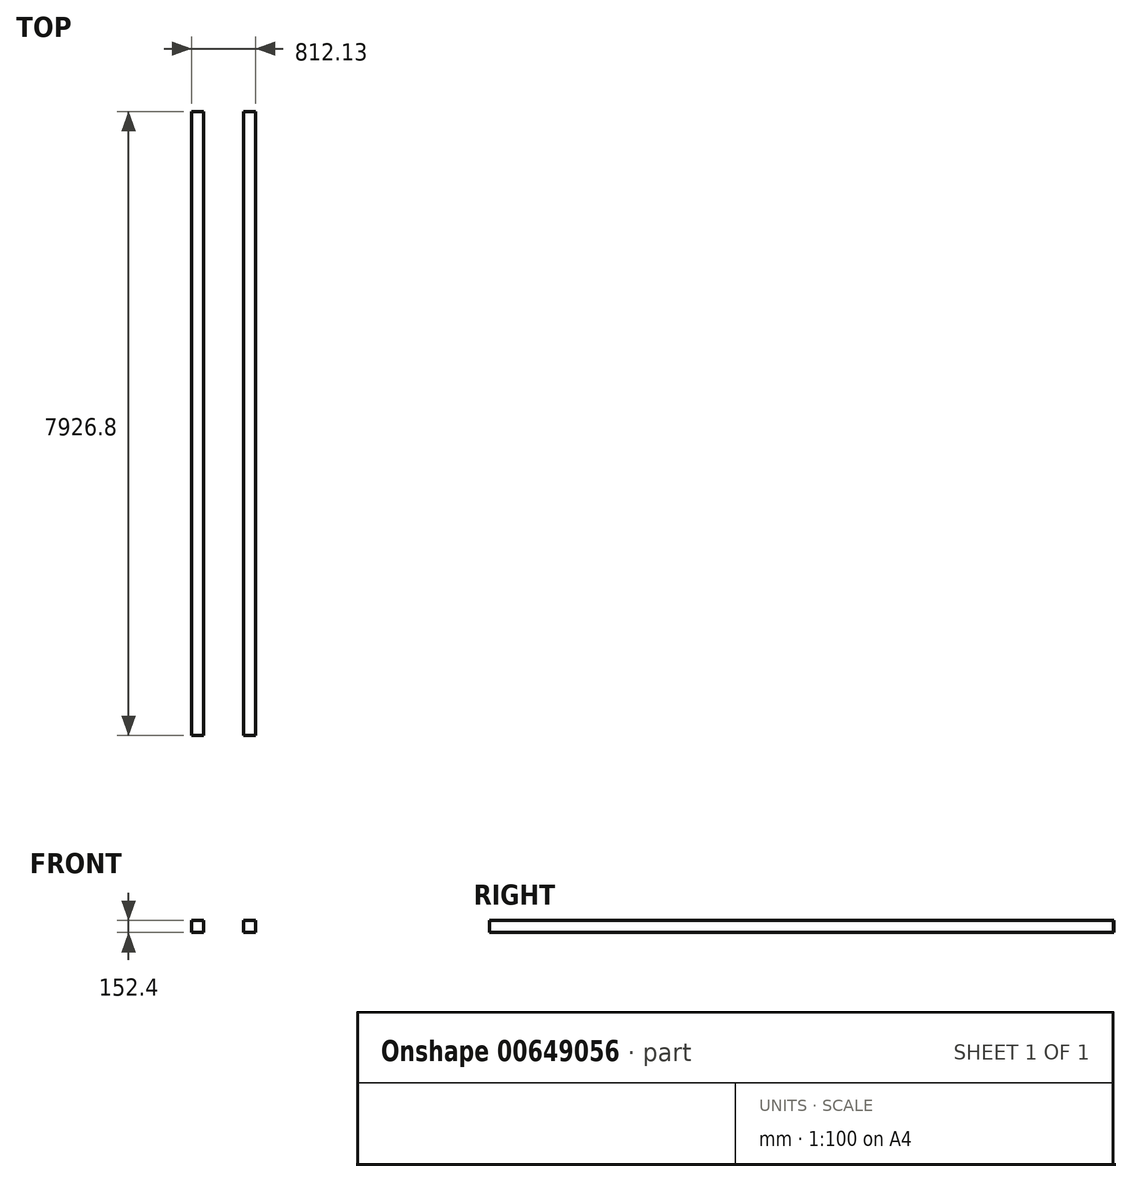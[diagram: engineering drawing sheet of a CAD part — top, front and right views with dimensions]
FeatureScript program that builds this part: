
annotation { "Feature Type Name" : "Feature", "Feature Type Description" : "" }
export const myFeature = defineFeature(function(context is Context, id is Id, definition is map)
    precondition{}
    {
        {
            var Q0;
            Q0=qCreatedBy(makeId("Top.planeOp"),FACE);
            var sketch = newSketch(context, id + "F0", { "sketchPlane" : qUnion([Q0])});
            skLineSegment(sketch, "E0.bottom", {"start": v(-434.17, 7458.07) * mm, "end": v(-281.77, 7458.07) * mm});
            skLineSegment(sketch, "E0.top", {"start": v(-434.17, -466.73) * mm, "end": v(-281.77, -466.73) * mm});
            skLineSegment(sketch, "E0.left", {"start": v(-434.17, 7458.07) * mm, "end": v(-434.17, -466.73) * mm});
            skLineSegment(sketch, "E0.right", {"start": v(-281.77, 7458.07) * mm, "end": v(-281.77, -466.73) * mm});
            skLineSegment(sketch, "E1.bottom", {"start": v(225.56, 7456.07) * mm, "end": v(377.96, 7456.07) * mm});
            skLineSegment(sketch, "E1.top", {"start": v(225.56, -468.73) * mm, "end": v(377.96, -468.73) * mm});
            skLineSegment(sketch, "E1.left", {"start": v(225.56, 7456.07) * mm, "end": v(225.56, -468.73) * mm});
            skLineSegment(sketch, "E1.right", {"start": v(377.96, 7456.07) * mm, "end": v(377.96, -468.73) * mm});
            skSolve(sketch);
        }
        {
            var Q0;
            Q0 = qSketchRegion(id + "F0", true);
            extrude(context, id + "F1", {"entities" : qUnion([Q0]), "depth" : 152.4 * mm, "offsetDistance" : 25.4 * mm});
        }
    });
